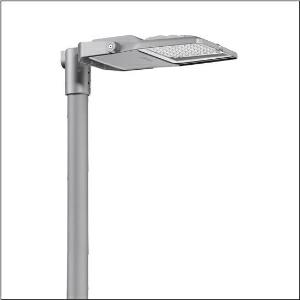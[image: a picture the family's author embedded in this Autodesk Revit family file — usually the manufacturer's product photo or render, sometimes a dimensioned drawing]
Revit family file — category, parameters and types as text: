
# Revit family: floodlight_fl_21_iq_mini___pl64_5xa7771b2e3a_ab64
name_source: partatom
category: Lighting Fixtures
units: mm (PartAtom-declared; Revit-internal decimal feet)

## family parameters
Cut with Voids When Loaded = No
Host = Face
Light Source = No
Part Type = Normal
Room Calculation Point = No
Round Connector Dimension = Use Diameter
Shared = No

## types (1)
- --- (1 x LED, 6020 lm, 45.5 W, 3000K)
    Apparent Load = 46 VA
    CIE Flux Codes = 28 80 98 100 100
    Color Rendering = 70
    Color Temperature = 3000K
    Default Elevation = 1800 mm
    Description = Floodlight FL 21 iQ mini, floodlight, primary light control with lens, of PMMA, primary optical cover: protective disc, of toughened safety glass, transparent, light distribution: PL64, light emission: direct distribution, installation type: surface-mounted, LED, High Power LED, rated luminous flux: 6.020lm, luminous efficacy: 132lm/W, light colour: 730, colour temperature: 3000K, control: Auto-Match, Temp-Guard, Lumen-Switch, Night-Set, Smart-Wire, Light-Fading, Desk-Remote (wireless, voltage-free reading and setting of iQ features in the workshop via application-optimized NFC function/RFID function), optimised constant luminous flux control (CLO 2.0), with terminal, 6-pole, mains connection: 220..240V, AC, 50/60Hz, start of lifetime: 46W, end of service life: 48W, reduction: 22W, luminaire housing, of diecast aluminium, powder-coated, Siteco® metallic grey (DB 702S), corrosivity category C5 mid according to DIN EN ISO 12944, sealing non-destructively replaceable, please order mast flange separately, mast bracket, of steel, galvanised, powder-coated, Siteco® metallic grey (DB 702S), protection rating (complete): IP66, insulation class (complete): insulation class II (safety insulation), certification: CE, ENEC, VDE, protection symbol: D, impact resistance: IK08, permissible operating ambient temperature: -40..+40°C, permissible operating ambient temperature for outdoor applications: -40..+50°C, standard: DIN EN 12944, LABS conformity tested according to VDMA 24364:2018-05, packaging unit: 1 piece

Light Distribution: PL64
    Height = 70 mm
    Lamp = 1 x LED
    Lamp Light Flux = 6020 lm
    Lamp Power = 45.5 W
    Lamp count = 1
    Length = 485 mm
    Luminous efficacy = 132 lm/W
    Manufacturer = Siteco
    ModVariant = No
    Model = 5XA7771B2E3A
    Number of Poles = 1
    OnlyDefault = Yes
    Power Factor = 1
    Product Name = Floodlight FL 21 iQ mini | PL64
    Product group = floodlight | pylon annexe
    ProductGroupID = 6200
    Protection Class = Protection class II
    Protection Degree = IP 66
    RLX_Detail_Level = 1
    RLX_Emergency_Light_Flux = 0 lm
    RLX_Emergency_Type = 0
    RLX_Emergency_Type_DB = No
    RlxData = <blob elided: 101217 chars, md5=b718981a>
    Socket = socket
    Standby Power = 0 W
    System Light Flux = 6020 lm
    System Power = 46 W
    Type Comments = factory setting: luminous flux: 100 % | dim-lin: 254 | 463 mA
    Type Image = l_1007125.jpg
    URL = http://relux.com
    VarID = @adj_137487
    Voltage = 0 V
    Weight = 0.00 kg
    Width = 337 mm

## geometry (parser evidence)
native form markers: Blend x4, Sweep x14
no freeform markers — native parametric forms only
